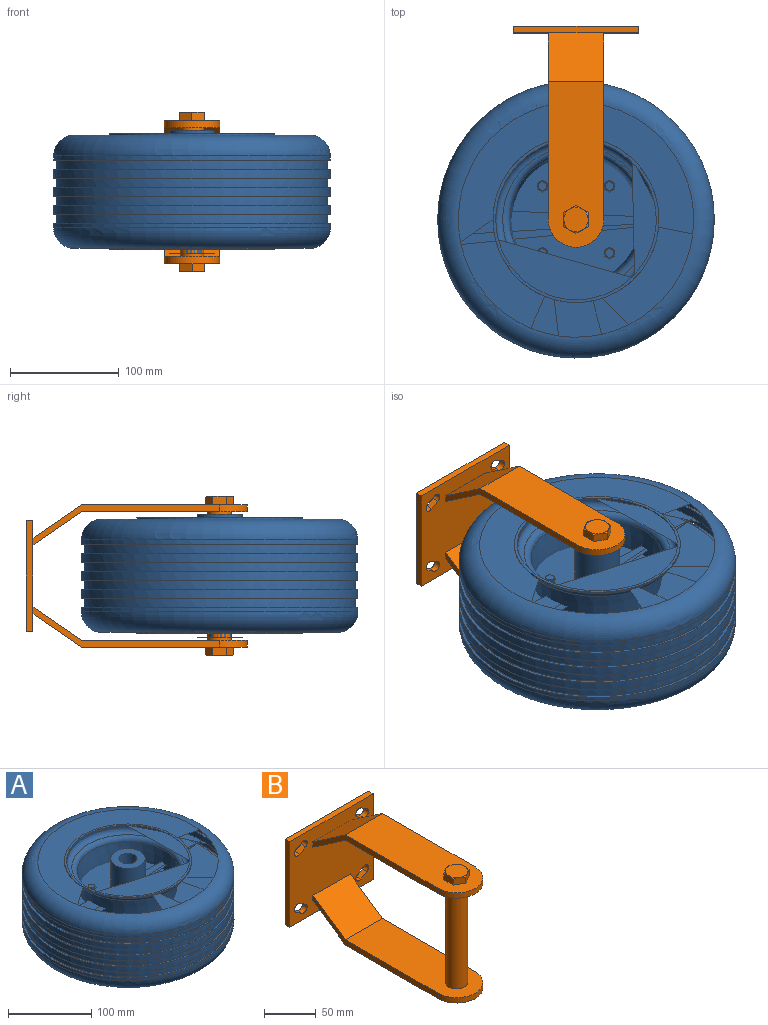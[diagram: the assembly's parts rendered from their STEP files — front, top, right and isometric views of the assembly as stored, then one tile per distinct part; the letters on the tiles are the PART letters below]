
ASSEMBLY  parts=2 mates=1
PART A: 102 faces, bbox 274.9x274.9x113 mm
  f0: plane 7.94x7.94mm, normal (0,0,1), area 49.5mm2, adj f1
  f1: cylinder r=3.97mm len=7.94mm, axis (0,0,-1), area 63.3mm2, adj f0,f2
  f2: plane 11x9.53mm, normal (0,0,1), area 29.1mm2, adj f1,f3,f79,f80,f81,f82,f83
  f3: plane 4.76x4.76mm, normal (-0.5,-0.87,0), area 26.2mm2, adj f2,f4,f79,f83
  f4: plane 86.81x86.56mm, normal (0,0,1), area 3535.7mm2, adj f3,f5,f9,f10,f11,f12,f13,f14
  f5: plane 4.76x4.76mm, normal (-0.5,-0.87,0), area 26.2mm2, adj f4,f6,f9,f13
  f6: plane 11x9.53mm, normal (0,0,1), area 29.1mm2, adj f5,f7,f9,f10,f11,f12,f13
  f7: cylinder r=3.97mm len=7.94mm, axis (0,0,-1), area 63.3mm2, adj f6,f8
  f8: plane 8.08x7.94mm, normal (0,0,1), area 49.5mm2, adj f7
  f9: plane 4.76x4.76mm, normal (0.5,-0.87,0), area 26.2mm2, adj f4,f5,f6,f10
  f10: plane 5.5x4.76mm, normal (1,0,0), area 26.2mm2, adj f4,f6,f9,f11
  f11: plane 4.76x4.76mm, normal (0.5,0.87,0), area 26.2mm2, adj f4,f6,f10,f12
  f12: plane 4.76x4.76mm, normal (-0.5,0.87,0), area 26.2mm2, adj f4,f6,f11,f13
  f13: plane 5.5x4.76mm, normal (-1,0,0), area 26.2mm2, adj f4,f5,f6,f12
  f14: cylinder r=27.66mm len=37.32mm, axis (0,0,-1), area 260.1mm2, adj f4,f15,f34,f40
  f15: plane 77.74x23.34mm, normal (0,0,1), area 909.1mm2, adj f14,f16,f34,f40
  f16: torus R=54.97mm, axis (0,0,1), area 1684.7mm2, adj f15,f17,f18,f19,f20
  f17: plane 77.74x23.6mm, normal (0,0,1), area 909.1mm2, adj f16,f34,f35,f36
  f18: plane 77.74x22.89mm, normal (0,0,1), area 909.1mm2, adj f16,f36,f37,f38
  f19: plane 77.74x23.6mm, normal (0,0,1), area 909.1mm2, adj f16,f38,f39,f40
  f20: cone r=60.98mm half-angle=5deg, axis (0,0,1), area 12238.7mm2, adj f16,f21
  f21: torus R=67.31mm, axis (0,0,1), area 3752.8mm2, adj f20,f22
  f22: torus R=67.31mm, axis (0,0,1), area 4471.8mm2, adj f21,f23
  f23: cylinder r=73.66mm len=147.32mm, axis (0,0,1), area 1469.5mm2, adj f22,f24
  f24: plane 155.22x152.41mm, normal (0,0,1), area 1195.8mm2, adj f23,f25
  f25: cylinder r=76.2mm len=152.4mm, axis (0,0,1), area 608mm2, adj f24,f26
  f26: plane 220.13x216.14mm, normal (0,0,1), area 9325.8mm2, adj f25,f27
  f27: torus R=108.07mm, axis (0,0,1), area 22447.5mm2, adj f26,f28
  f28: cylinder r=127mm len=254mm, axis (0,0,1), area 3305.1mm2, adj f27,f29
  f29: plane 258.7x254.01mm, normal (0,0,-1), area 1882.3mm2, adj f28,f30
  f30: cylinder r=124.62mm len=249.24mm, axis (0,0,1), area 6486.3mm2, adj f29,f31
  f31: plane 258.7x254.01mm, normal (0,0,1), area -22511.7mm2, adj f30,f32
  f32: cylinder r=127mm len=254mm, axis (0,0,1), area 6610.2mm2, adj f31,f33
  f33: plane 258.7x254.01mm, normal (0,0,-1), area 76005.9mm2, adj f32
  f34: cylinder r=14.63mm len=24.5mm, axis (0,0,-1), area 283.5mm2, adj f4,f14,f15,f17,f35
  f35: cylinder r=27.66mm len=37.32mm, axis (0,0,-1), area 260.1mm2, adj f4,f17,f34,f36
  f36: cylinder r=14.63mm len=24.5mm, axis (0,0,-1), area 283.5mm2, adj f4,f17,f18,f35,f37
  f37: cylinder r=27.66mm len=37.32mm, axis (0,0,-1), area 260.1mm2, adj f4,f18,f36,f38
  f38: cylinder r=14.63mm len=24.5mm, axis (0,0,-1), area 283.5mm2, adj f4,f18,f19,f37,f39
  f39: cylinder r=27.66mm len=37.32mm, axis (0,0,-1), area 260.1mm2, adj f4,f19,f38,f40
  f40: cylinder r=14.63mm len=24.5mm, axis (0,0,-1), area 283.5mm2, adj f4,f14,f15,f19,f39
  f41: cylinder r=20.64mm len=47.63mm, axis (0,0,1), area 6175.5mm2, adj f4,f42
  f42: plane 42.04x41.28mm, normal (0,0,1), area 971.9mm2, adj f41,f43
  f43: cylinder r=10.79mm len=113.03mm, axis (0,0,1), area 7666.5mm2, adj f42,f44
  f44: plane 42.04x41.28mm, normal (0,0,-1), area 1640.9mm2, adj f43,f45
  f45: cylinder r=20.64mm len=53.98mm, axis (0,0,1), area 6998.9mm2, adj f44,f46
  f46: plane 111.98x109.95mm, normal (0,0,-1), area 7648.5mm2, adj f45,f47,f49,f51,f57,f59
  f47: cylinder r=6.35mm len=12.7mm, axis (0,0,1), area 190mm2, adj f46,f48
  f48: plane 12.7x12.7mm, normal (0,0,-1), area 126.7mm2, adj f47
  f49: cylinder r=6.35mm len=12.7mm, axis (0,0,1), area 190mm2, adj f46,f50
  f50: plane 12.94x12.7mm, normal (0,0,-1), area 126.7mm2, adj f49
  f51: torus R=54.97mm, axis (0,0,1), area 1684.7mm2, adj f46,f52
  f52: cone r=58.13mm half-angle=5deg, axis (0,0,-1), area 12238.7mm2, adj f51,f53
  f53: torus R=67.31mm, axis (0,0,1), area 3752.8mm2, adj f52,f54
  f54: torus R=67.31mm, axis (0,0,1), area 4471.8mm2, adj f53,f55
  f55: cylinder r=73.66mm len=147.32mm, axis (0,0,1), area 1469.5mm2, adj f54,f56
  f56: plane 150.05x147.32mm, normal (0,0,1), area 17045.6mm2, adj f55
  f57: cylinder r=6.35mm len=12.7mm, axis (0,0,1), area 190mm2, adj f46,f58
  f58: plane 12.7x12.7mm, normal (0,0,-1), area 126.7mm2, adj f57
  f59: cylinder r=6.35mm len=12.7mm, axis (0,0,1), area 190mm2, adj f46,f60
  f60: plane 12.7x12.7mm, normal (0,0,-1), area 126.7mm2, adj f59
  f61: plane 5.5x4.76mm, normal (1,0,0), area 26.2mm2, adj f4,f62,f65,f69
  f62: plane 11x9.53mm, normal (0,0,1), area 29.1mm2, adj f61,f63,f65,f66,f67,f68,f69
  f63: cylinder r=3.97mm len=7.94mm, axis (0,0,-1), area 63.3mm2, adj f62,f64
  f64: plane 7.94x7.94mm, normal (0,0,1), area 49.5mm2, adj f63
  f65: plane 4.76x4.76mm, normal (0.5,0.87,0), area 26.2mm2, adj f4,f61,f62,f66
  f66: plane 4.76x4.76mm, normal (-0.5,0.87,0), area 26.2mm2, adj f4,f62,f65,f67
  f67: plane 5.5x4.76mm, normal (-1,0,0), area 26.2mm2, adj f4,f62,f66,f68
  f68: plane 4.76x4.76mm, normal (-0.5,-0.87,0), area 26.2mm2, adj f4,f62,f67,f69
  f69: plane 4.76x4.76mm, normal (0.5,-0.87,0), area 26.2mm2, adj f4,f61,f62,f68
  f70: plane 5.5x4.76mm, normal (-1,0,0), area 26.2mm2, adj f4,f71,f74,f78
  f71: plane 11x9.53mm, normal (0,0,1), area 29.1mm2, adj f70,f72,f74,f75,f76,f77,f78
  f72: cylinder r=3.97mm len=7.94mm, axis (0,0,-1), area 63.3mm2, adj f71,f73
  f73: plane 7.94x7.94mm, normal (0,0,1), area 49.5mm2, adj f72
  f74: plane 4.76x4.76mm, normal (-0.5,-0.87,0), area 26.2mm2, adj f4,f70,f71,f75
  f75: plane 4.76x4.76mm, normal (0.5,-0.87,0), area 26.2mm2, adj f4,f71,f74,f76
  f76: plane 5.5x4.76mm, normal (1,0,0), area 26.2mm2, adj f4,f71,f75,f77
  f77: plane 4.76x4.76mm, normal (0.5,0.87,0), area 26.2mm2, adj f4,f71,f76,f78
  f78: plane 4.76x4.76mm, normal (-0.5,0.87,0), area 26.2mm2, adj f4,f70,f71,f77
  f79: plane 5.5x4.76mm, normal (-1,0,0), area 26.2mm2, adj f2,f3,f4,f80
  f80: plane 4.76x4.76mm, normal (-0.5,0.87,0), area 26.2mm2, adj f2,f4,f79,f81
  f81: plane 4.76x4.76mm, normal (0.5,0.87,0), area 26.2mm2, adj f2,f4,f80,f82
  f82: plane 5.5x4.76mm, normal (1,0,0), area 26.2mm2, adj f2,f4,f81,f83
  f83: plane 4.76x4.76mm, normal (0.5,-0.87,0), area 26.2mm2, adj f2,f3,f4,f82
  f84: plane 253.85x249.25mm, normal (0,0,-1), area 48788.2mm2, adj f85
  f85: cylinder r=124.62mm len=249.24mm, axis (0,0,1), area 6486.3mm2, adj f84,f86
  f86: plane 258.7x254.01mm, normal (0,0,-1), area -22511.7mm2, adj f85,f87
  f87: cylinder r=127mm len=254mm, axis (0,0,1), area 3305.1mm2, adj f86,f88
  f88: torus R=108.07mm, axis (0,0,1), area 22447.5mm2, adj f87,f89
  f89: plane 220.13x216.14mm, normal (0,0,1), area 18446.4mm2, adj f88,f90
  f90: cylinder r=76.2mm len=152.4mm, axis (0,0,1), area 608mm2, adj f89,f91
  f91: plane 155.22x152.41mm, normal (0,0,1), area 27362.1mm2, adj f90
  f92: plane 253.85x249.25mm, normal (0,0,1), area 48788.2mm2, adj f93
  f93: cylinder r=124.62mm len=249.24mm, axis (0,0,1), area 6486.3mm2, adj f92,f94
  f94: plane 258.7x254.01mm, normal (0,0,1), area -22511.7mm2, adj f93,f95
  f95: cylinder r=127mm len=254mm, axis (0,0,1), area 6610.2mm2, adj f94,f96
  f96: plane 258.7x254.01mm, normal (0,0,-1), area 76005.9mm2, adj f95
  f97: plane 253.85x249.25mm, normal (0,0,1), area 48788.2mm2, adj f98
  f98: cylinder r=124.62mm len=249.24mm, axis (0,0,1), area 6486.3mm2, adj f97,f99
  f99: plane 258.7x254.01mm, normal (0,0,1), area -22511.7mm2, adj f98,f100
  f100: cylinder r=127mm len=254mm, axis (0,0,1), area 6610.2mm2, adj f99,f101
  f101: plane 258.7x254.01mm, normal (0,0,-1), area 76005.9mm2, adj f100
PART B: 63 faces, bbox 116.6x205.9x149 mm
  f0: plane 22.41x22.23mm, normal (0,0,-1), area 387.9mm2, adj f2,f3,f4,f5,f6,f7
  f1: plane 22.41x22.23mm, normal (0,0,1), area 387.9mm2, adj f8,f9,f10,f11,f12,f13
  f2: cone r=11.11mm half-angle=60deg, axis (0,0,1), area 12.1mm2, adj f0,f14,f15
  f3: cone r=11.11mm half-angle=60deg, axis (0,0,1), area 12.1mm2, adj f0,f15,f16
  f4: cone r=11.11mm half-angle=60deg, axis (0,0,1), area 12.1mm2, adj f0,f16,f17
  f5: cone r=11.11mm half-angle=60deg, axis (0,0,1), area 12.1mm2, adj f0,f17,f18
  f6: cone r=11.11mm half-angle=60deg, axis (0,0,1), area 12.1mm2, adj f0,f18,f19
  f7: cone r=11.11mm half-angle=60deg, axis (0,0,1), area 12.1mm2, adj f0,f14,f19
  f8: cone r=11.11mm half-angle=60deg, axis (0,0,-1), area 12.1mm2, adj f1,f20,f21
  f9: cone r=11.11mm half-angle=60deg, axis (0,0,-1), area 12.1mm2, adj f1,f21,f22
  f10: cone r=11.11mm half-angle=60deg, axis (0,0,-1), area 12.1mm2, adj f1,f22,f23
  f11: cone r=11.11mm half-angle=60deg, axis (0,0,-1), area 12.1mm2, adj f1,f23,f24
  f12: cone r=11.11mm half-angle=60deg, axis (0,0,-1), area 12.1mm2, adj f1,f20,f25
  f13: cone r=11.11mm half-angle=60deg, axis (0,0,-1), area 12.1mm2, adj f1,f24,f25
  f14: plane 13.89x9mm, normal (1,0,0), area 97.5mm2, adj f2,f7,f15,f19,f27
  f15: plane 12.17x8.99mm, normal (0.5,-0.87,0), area 97.5mm2, adj f2,f3,f14,f16,f27
  f16: plane 12.17x8.99mm, normal (-0.5,-0.87,0), area 97.5mm2, adj f3,f4,f15,f17,f27
  f17: plane 13.89x9mm, normal (-1,0,0), area 97.5mm2, adj f4,f5,f16,f18,f27
  f18: plane 12.17x8.99mm, normal (-0.5,0.87,0), area 97.5mm2, adj f5,f6,f17,f19,f27
  f19: plane 12.17x8.99mm, normal (0.5,0.87,0), area 97.5mm2, adj f6,f7,f14,f18,f27
  f20: plane 13.39x10.21mm, normal (-0.5,0.87,0), area 97.5mm2, adj f8,f12,f21,f25,f30
  f21: plane 15.11x10.21mm, normal (-1,0,0), area 97.5mm2, adj f8,f9,f20,f22,f30
  f22: plane 13.39x10.21mm, normal (-0.5,-0.87,0), area 97.5mm2, adj f9,f10,f21,f23,f30
  f23: plane 13.39x10.21mm, normal (0.5,-0.87,0), area 97.5mm2, adj f10,f11,f22,f24,f30
  f24: plane 15.11x10.21mm, normal (1,0,0), area 97.5mm2, adj f11,f13,f23,f25,f30
  f25: plane 13.39x10.21mm, normal (0.5,0.87,0), area 97.5mm2, adj f12,f13,f20,f24,f30
  f26: cylinder r=10.79mm len=118.11mm, axis (0,0,-1), area 8011mm2, adj f29,f32
  f27: plane 152.87x50.8mm, normal (0,0,-1), area 7037.2mm2, adj f14,f15,f16,f17,f18,f19,f28,f33
  f28: cylinder r=25.4mm len=50.8mm, axis (0,0,-1), area 506.7mm2, adj f27,f29,f33,f35
  f29: plane 152.87x50.8mm, normal (0,0,1), area 7098.9mm2, adj f26,f28,f33,f35,f36
  f30: plane 152.87x50.8mm, normal (0,0,1), area 7037.2mm2, adj f20,f21,f22,f23,f24,f25,f31,f37
  f31: cylinder r=25.4mm len=50.8mm, axis (0,0,-1), area 506.7mm2, adj f30,f32,f37,f39
  f32: plane 152.87x50.8mm, normal (0,0,-1), area 6915.9mm2, adj f26,f31,f37,f39,f40
  f33: plane 171.45x36.84mm, normal (-1,0,0), area 1088.7mm2, adj f27,f28,f29,f34,f36,f61
  f34: plane 50.8x44.45mm, normal (0,0.57,-0.82), area 2738.1mm2, adj f27,f33,f35,f61
  f35: plane 171.45x36.84mm, normal (1,0,0), area 1088.7mm2, adj f27,f28,f29,f34,f36,f61
  f36: plane 50.8x44.45mm, normal (0,-0.57,0.82), area 2738.1mm2, adj f29,f33,f35,f61
  f37: plane 171.45x36.84mm, normal (1,0,0), area 1088.7mm2, adj f30,f31,f32,f38,f40,f61
  f38: plane 50.8x44.45mm, normal (0,0.57,0.82), area 2738.1mm2, adj f30,f37,f39,f61
  f39: plane 171.45x36.84mm, normal (-1,0,0), area 1088.7mm2, adj f30,f31,f32,f38,f40,f61
  f40: plane 50.8x44.45mm, normal (0,-0.57,-0.82), area 2738.1mm2, adj f32,f37,f39,f61
  f41: cylinder r=4.76mm len=8.85mm, axis (0,1,0), area 95mm2, adj f42,f59,f60,f61
  f42: plane 7.94x6.35mm, normal (0.51,0,0.86), area 58.8mm2, adj f41,f60,f61,f62
  f43: cylinder r=4.76mm len=8.85mm, axis (0,1,0), area 95mm2, adj f44,f46,f60,f61
  f44: plane 7.94x6.35mm, normal (0.51,0,-0.86), area 58.8mm2, adj f43,f45,f60,f61
  f45: cylinder r=4.76mm len=8.85mm, axis (0,1,0), area 95mm2, adj f44,f46,f60,f61
  f46: plane 7.94x6.35mm, normal (-0.51,0,0.86), area 58.8mm2, adj f43,f45,f60,f61
  f47: cylinder r=4.76mm len=8.85mm, axis (0,1,0), area 95mm2, adj f48,f50,f60,f61
  f48: plane 7.94x6.35mm, normal (-0.51,0,0.86), area 58.8mm2, adj f47,f49,f60,f61
  f49: cylinder r=4.76mm len=8.85mm, axis (0,1,0), area 95mm2, adj f48,f50,f60,f61
  f50: plane 7.94x6.35mm, normal (0.51,0,-0.86), area 58.8mm2, adj f47,f49,f60,f61
  f51: cylinder r=4.76mm len=8.85mm, axis (0,1,0), area 95mm2, adj f52,f54,f60,f61
  f52: plane 7.94x6.35mm, normal (0.51,0,0.86), area 58.8mm2, adj f51,f53,f60,f61
  f53: cylinder r=4.76mm len=8.85mm, axis (0,1,0), area 95mm2, adj f52,f54,f60,f61
  f54: plane 7.94x6.35mm, normal (-0.51,0,-0.86), area 58.8mm2, adj f51,f53,f60,f61
  f55: plane 101.6x6.35mm, normal (-1,0,0), area 645.2mm2, adj f56,f58,f60,f61
  f56: plane 114.3x6.35mm, normal (0,0,1), area 725.8mm2, adj f55,f57,f60,f61
  f57: plane 101.6x6.35mm, normal (1,0,0), area 645.2mm2, adj f56,f58,f60,f61
  f58: plane 114.3x6.35mm, normal (0,0,-1), area 725.8mm2, adj f55,f57,f60,f61
  f59: plane 7.94x6.35mm, normal (-0.51,0,-0.86), area 58.8mm2, adj f41,f60,f61,f62
  f60: plane 114.3x101.6mm, normal (0,1,0), area 10975.2mm2, adj f41,f42,f43,f44,f45,f46,f47,f48
  f61: plane 114.3x101.6mm, normal (0,-1,0), area 10330mm2, adj f33,f34,f35,f36,f37,f38,f39,f40
  f62: cylinder r=4.76mm len=8.85mm, axis (0,1,0), area 95mm2, adj f42,f59,f60,f61
PLACE A t=(0,0,0.22)mm
PLACE B at identity fixed
MATE slider A.f16 <-> B.f2  axis (0,0,1) through (0,-177.8,56.73)mm
